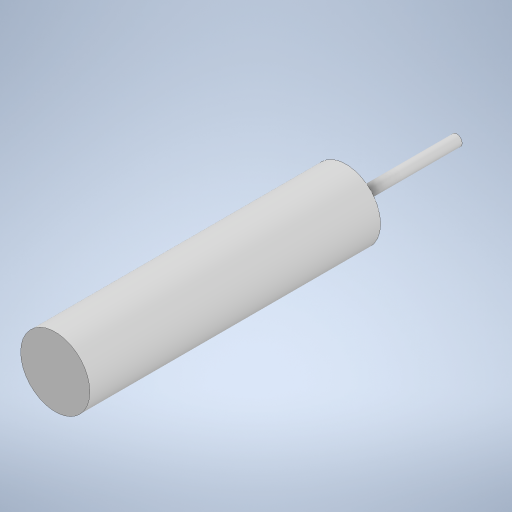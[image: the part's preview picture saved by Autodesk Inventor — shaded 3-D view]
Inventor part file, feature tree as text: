
AUTODESK INVENTOR PART (.ipt)
format: ipt  version: 2024 (Build 280153000, 153)  size: 227,840 bytes
history: native  units: in
note: dims shown in document units (in); Inventor stores cm internally (conversion verified against a paired STEP export)
features: extrude x2, sketch x2
ambient origin geometry x8: Origin, YZ Plane, XZ Plane, XY Plane, X Axis, Y Axis, Z Axis, Center Point
bodies: Solid1 (feature_tree)
feature tree (4):
  extrude  "Extrusion1"  Depth=0.4134in TaperAngle=0.0deg
  extrude  "Extrusion2"  Depth=0.1575in TaperAngle=0.0deg
  sketch  "Sketch1"  dims[d0=0.0984in d1=0.4134in d2=0.0in]
  sketch  "Sketch2"  dims[d3=0.0157in d4=0.1575in d5=0.0in]
